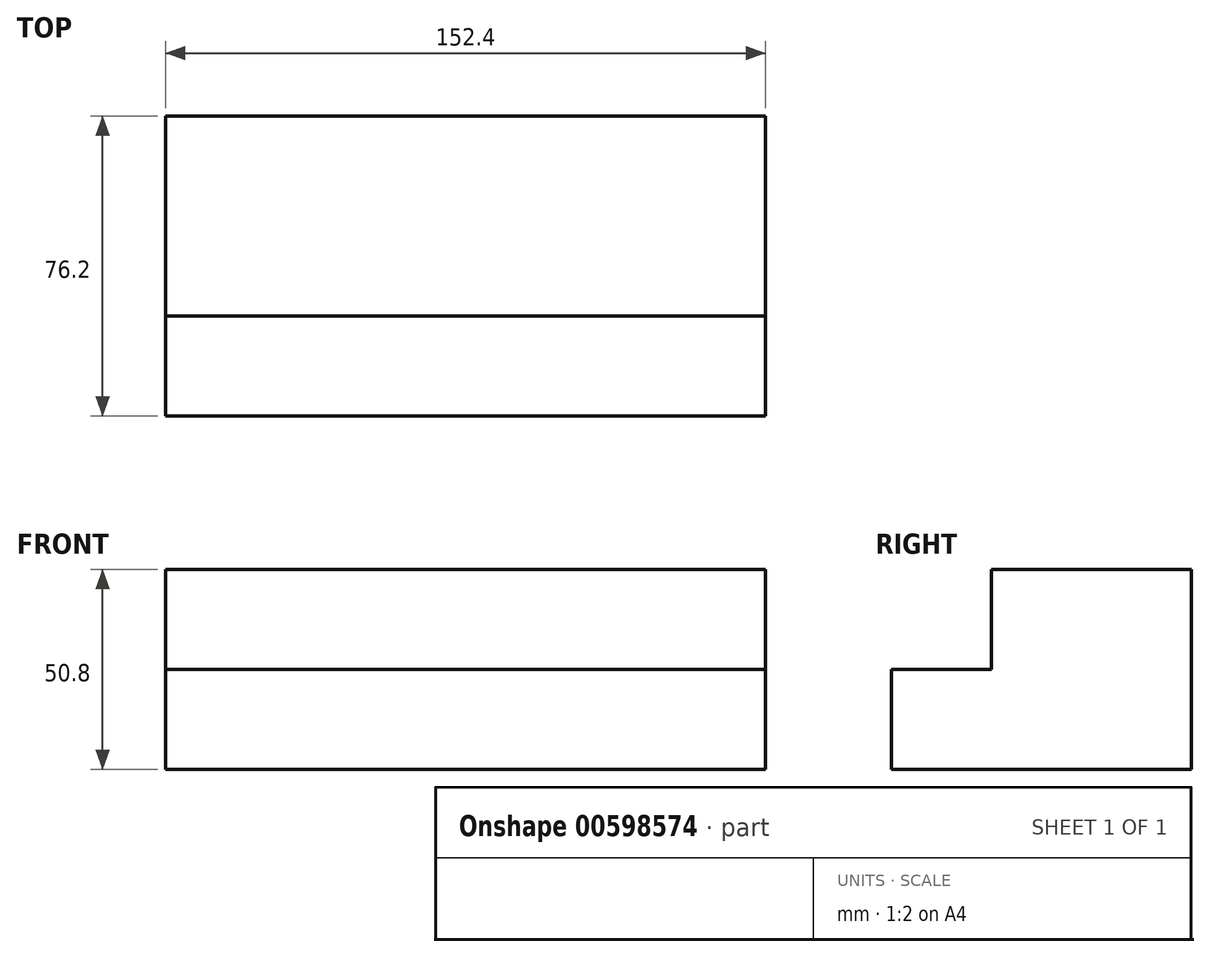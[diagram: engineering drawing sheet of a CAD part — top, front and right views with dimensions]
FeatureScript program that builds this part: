
annotation { "Feature Type Name" : "Feature", "Feature Type Description" : "" }
export const myFeature = defineFeature(function(context is Context, id is Id, definition is map)
    precondition{}
    {
        {
            var Q0;
            Q0=qCreatedBy(makeId("Right.planeOp"),FACE);
            var sketch = newSketch(context, id + "F0", { "sketchPlane" : qUnion([Q0])});
            skLineSegment(sketch, "E0", {"start": v(0, 0) * mm, "end": v(76.2, 0) * mm});
            skLineSegment(sketch, "E1", {"start": v(76.2, 0) * mm, "end": v(76.2, 50.8) * mm});
            skLineSegment(sketch, "E2", {"start": v(76.2, 50.8) * mm, "end": v(25.4, 50.8) * mm});
            skLineSegment(sketch, "E3", {"start": v(25.4, 50.8) * mm, "end": v(25.4, 25.4) * mm});
            skLineSegment(sketch, "E4", {"start": v(25.4, 25.4) * mm, "end": v(0, 25.4) * mm});
            skLineSegment(sketch, "E5", {"start": v(0, 25.4) * mm, "end": v(0, 0) * mm});
            skSolve(sketch);
        }
        {
            var Q0;
            Q0=makeQuery(id+"F0.imprint","IMPRINT",FACE,{"disambiguationData":[TD([[makeQuery(id+"F0.imprint","IMPRINT",EDGE,{"derivedFrom":sQuery(id+"F0.wireOp",EDGE,"E0")}),1.0]])]});
            extrude(context, id + "F1", {"entities" : qUnion([Q0]), "depth" : 152.4 * mm, "offsetDistance" : 25.4 * mm});
        }
    });
